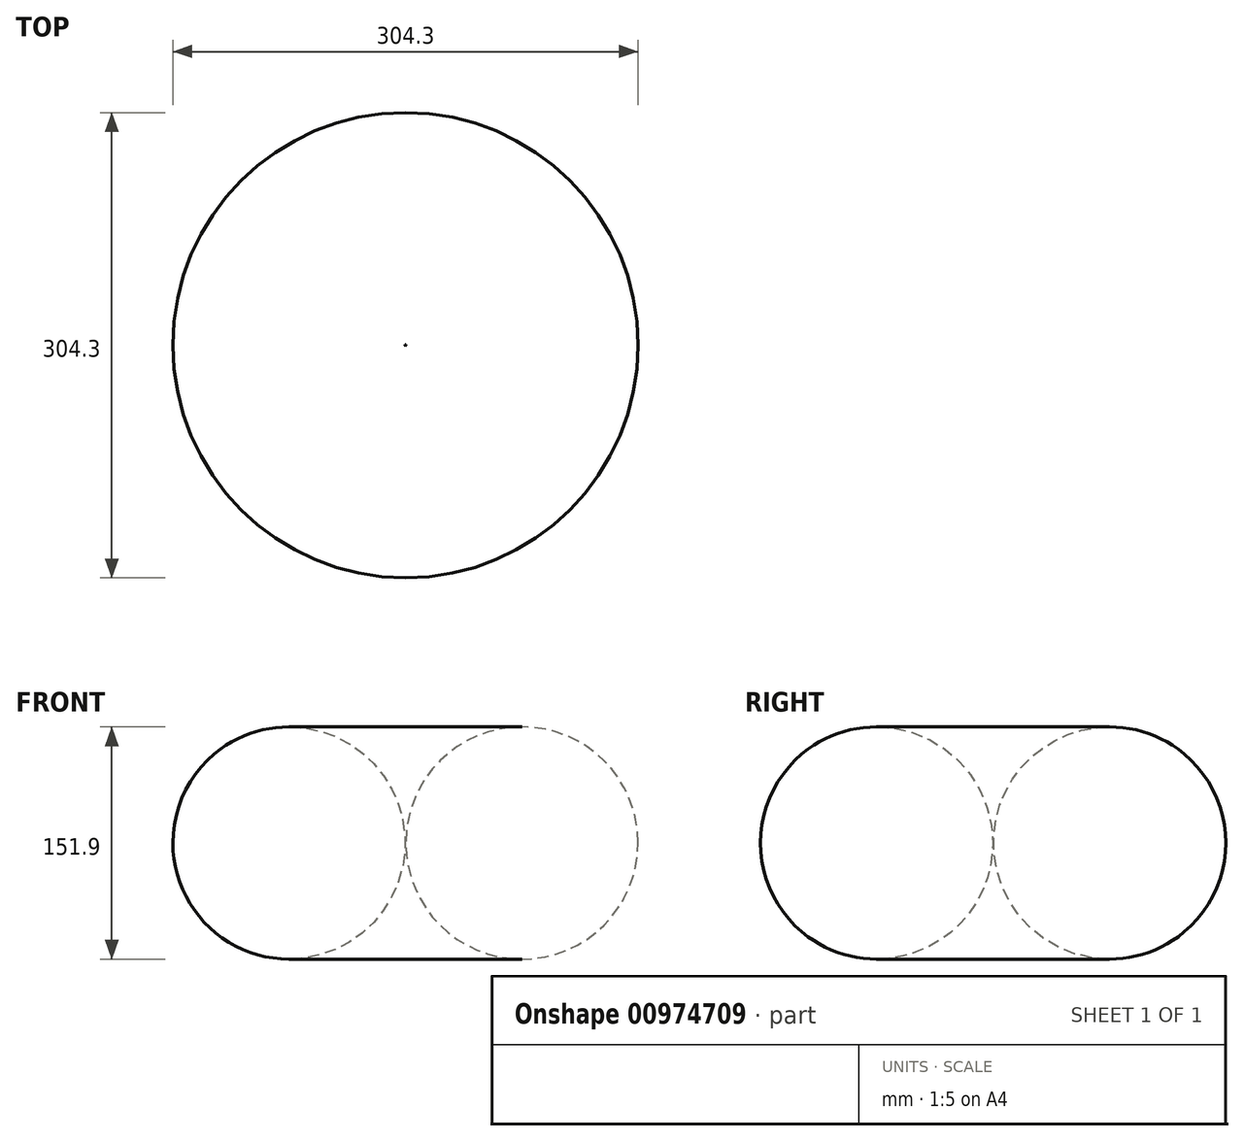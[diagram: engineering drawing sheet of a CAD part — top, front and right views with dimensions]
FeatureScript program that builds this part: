
annotation { "Feature Type Name" : "Feature", "Feature Type Description" : "" }
export const myFeature = defineFeature(function(context is Context, id is Id, definition is map)
    precondition{}
    {
        {
            var Q0;
            Q0=qCreatedBy(makeId("Front.planeOp"),FACE);
            var sketch = newSketch(context, id + "F0", { "sketchPlane" : qUnion([Q0])});
            skCircle(sketch, "E0", {"center": v(-76.2, 0) * mm, "radius": 75.95 * mm});
            skLineSegment(sketch, "E1", {"start": v(0, 52.8) * mm, "end": v(0, -37.26) * mm});
            skSolve(sketch);
        }
        {
            var Q0;
            Q0=makeQuery(id+"F0.imprint","IMPRINT",FACE,{"disambiguationData":[TD([[makeQuery(id+"F0.imprint","IMPRINT",EDGE,{"derivedFrom":sQuery(id+"F0.wireOp",EDGE,"E0")}),1.0]])]});
            var Q1;
            Q1=sQuery(id+"F0.wireOp",EDGE,"E1");
            revolve(context, id + "F1", {"surfaceOperationType" : NewSurfaceOperationType.NEW, "entities" : qUnion([Q0]), "axis" : qUnion([Q1]), "revolveType" : RevolveType.FULL});
        }
    });
